# Revit family: SJX1 FULLY UPHOLSTERED
name_source: partatom
category: Furniture
units: mm (PartAtom-declared; Revit-internal decimal feet)

## family parameters
Always vertical = Yes
Cut with Voids When Loaded = No
OmniClass Number = 23.40.00.00
OmniClass Title = Equipment and Furnishings
Room Calculation Point = No
Shared = No
Work Plane-Based = No

## types (1)
- SJX1
    Arms = No
    Assembly Code = E2020200
    Back = Gresham - Gabriel Byron 14101
    Black Plastic = Gresham - BLACK PLASTIC
    Frame = Gresham - Chrome
    LH Tablet = No
    Manufacturer = Gresham Office Furniture
    Model = SJX
    No Arms = Yes
    Plastics = Gresham - BLACK PLASTIC
    Product Brochure = http://gof.co.uk
    Product Code = SJX1
    Product Data Specification = http://gof.co.uk
    RH Tablet = No
    Range = SEATING
    Seat = Gresham - Gabriel Byron 14101
    URL = www.gof.co.uk

## geometry (parser evidence)
native form markers: Blend x4, Sweep x3
no freeform markers — native parametric forms only
